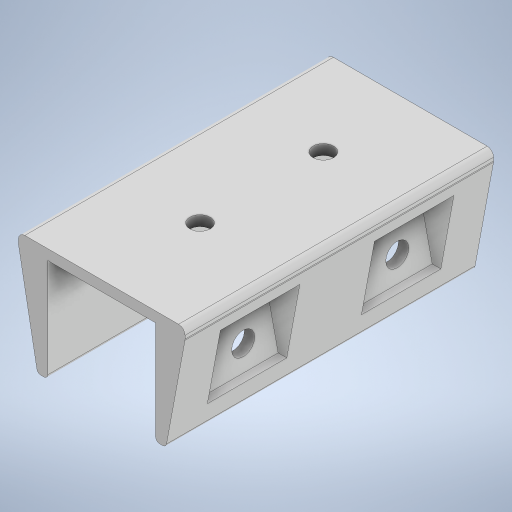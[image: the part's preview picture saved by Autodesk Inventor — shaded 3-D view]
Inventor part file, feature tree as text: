
AUTODESK INVENTOR PART (.ipt)
format: ipt  version: 2024.1 (Build 281209000, 209)  size: 372,736 bytes
history: native  units: mm
features: sketch x5, extrude x3, plane x3, chamfer x3, hole x2, fillet x2, mirror x2, projected_geometry x2
ambient origin geometry x8: Origin, YZ Plane, XZ Plane, XY Plane, X Axis, Y Axis, Z Axis, Center Point
bodies: Body1 (feature_tree)
feature tree (22):
  extrude  "Extrusion2"  Depth=60.07774mm
  hole  "Hole1"  [1 undecoded]
  extrude  "Extrusion3"  Depth=2.0mm
  fillet  "Fillet1"  Radius=2.0mm
  fillet  "Fillet2"  Radius=10.5mm
  plane  "Work Plane3"
  extrude  "Extrusion4"  Depth=20.0mm
  hole  "Hole2"  [1 undecoded]
  plane  "Work Plane4"
  mirror  "Mirror2"
  mirror  "Mirror3"
  chamfer  "Chamfer1"  Distance=0.75mm
  chamfer  "Chamfer2"  Distance=1.25mm
  chamfer  "Chamfer3"  Distance=15.0mm
  sketch  "Sketch1"  dims[d27=24.0mm d28=60.07774mm]
  sketch  "Sketch2"  dims[d29=32.44mm d30=19.14674mm]
  sketch  "Sketch3"  dims[d31=16.22mm d32=3.458734mm d33=2.0mm d34=0.0mm]
  plane  "Work Plane2"
  sketch  "Sketch4"  dims[d35=4.0mm d36=6.0mm d37=4.0mm d38=2.0mm d39=90.0deg d40=8.0mm d41=20.594885mm d42=10.5mm]
  sketch  "Sketch5"  dims[d43=2.0mm d44=20.0mm d45=2.0mm d46=0.0mm d47=0.75mm d48=1.25mm d50=15.0mm d51=2.0mm d52=10.0mm d53=5.0mm d54=10.0mm d55=0.0mm d56=4.5mm d57=6.0mm d58=8.0mm d59=4.0mm d60=90.0deg d61=8.0mm d62=20.594885mm d63=5.0mm d64=5.0mm d65=2.73mm d66=2.0mm d67=45.0deg d68=2.79mm d69=2.0mm d70=45.0deg d71=0.93mm d72=2.0mm d73=45.0deg d49=0.0mm]
  projected_geometry  "Project Cut Edges1"
  projected_geometry  "Project Cut Edges2"
note: 2 required parameter values undecoded (feature->parameter linkage not recoverable at this tier; creation-order binding heuristic only, values carry confidence <= 0.55)
